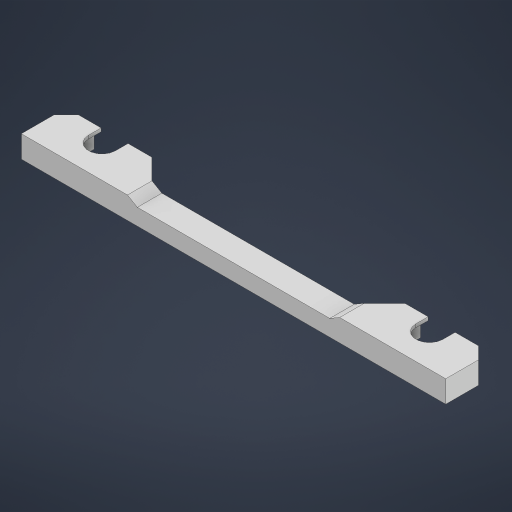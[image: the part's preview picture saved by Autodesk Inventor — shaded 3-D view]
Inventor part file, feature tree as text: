
AUTODESK INVENTOR PART (.ipt)
format: ipt  version: 2024 (Build 280153000, 153)  size: 253,952 bytes
history: native  units: mm
features: extrude x3, sketch x3, projected_geometry x2, other x1
ambient origin geometry x8: Origin, YZ Plane, XZ Plane, XY Plane, X Axis, Y Axis, Z Axis, Center Point
bodies: Body1 (feature_tree)
feature tree (9):
  other  "Těleso1"
  extrude  "Vysunutí1"  Depth=5.2mm
  extrude  "Vysunutí2"  Depth=40.0mm
  extrude  "Vysunutí3"  Depth=4.0mm
  sketch  "Náčrt1"
  sketch  "Náčrt2"
  projected_geometry  "Promítnutá smyčka1"
  sketch  "Náčrt3"
  projected_geometry  "Promítnutá smyčka2"
